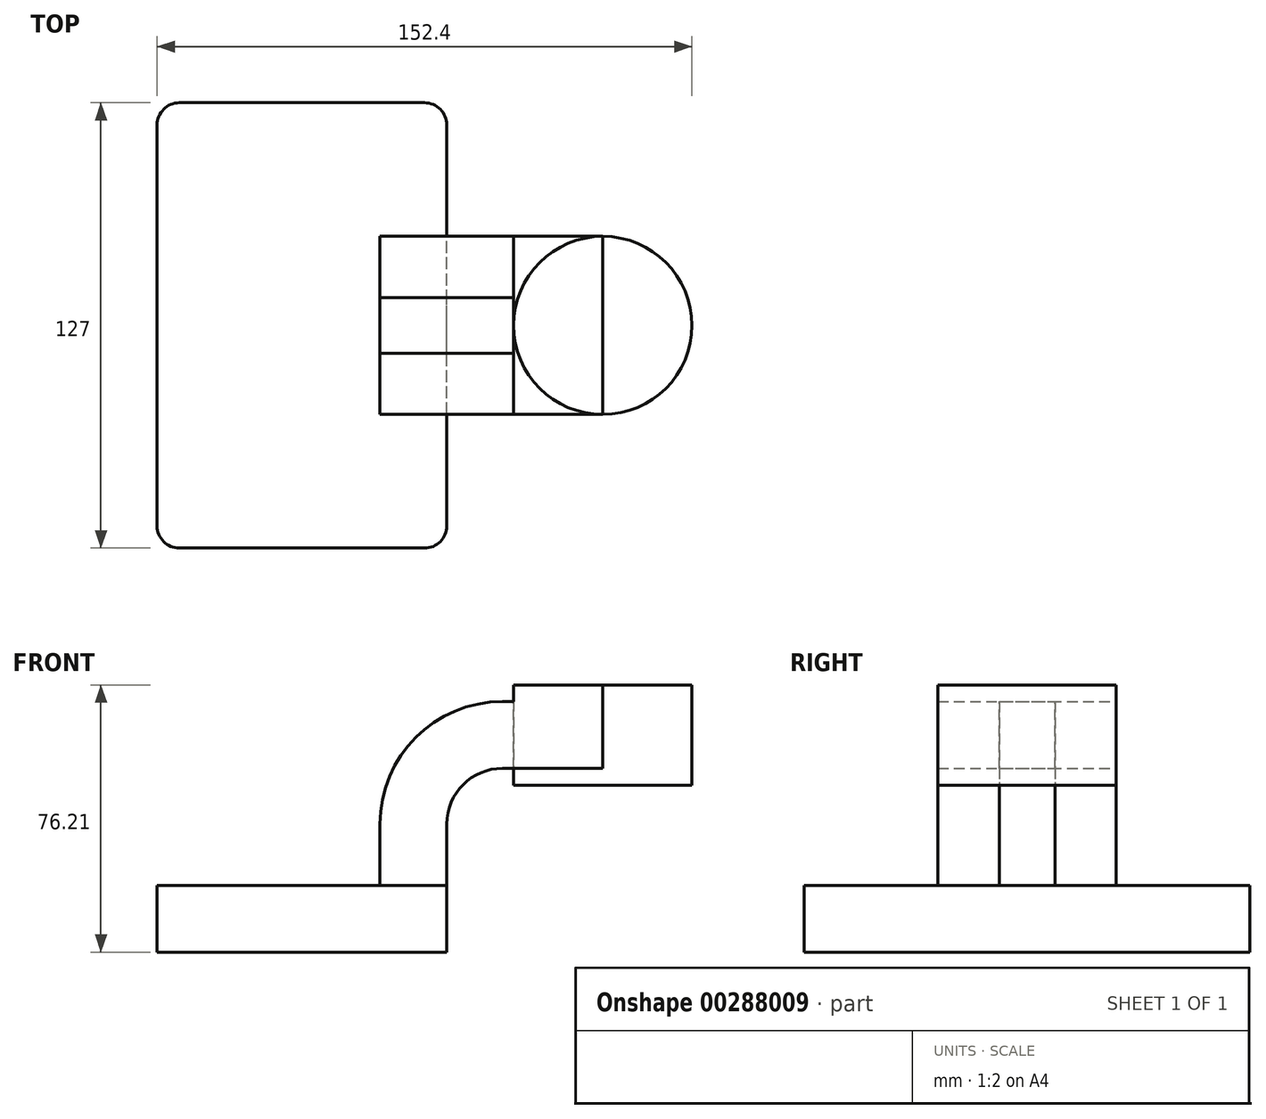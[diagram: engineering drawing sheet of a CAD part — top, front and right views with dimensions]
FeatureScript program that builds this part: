
annotation { "Feature Type Name" : "Feature", "Feature Type Description" : "" }
export const myFeature = defineFeature(function(context is Context, id is Id, definition is map)
    precondition{}
    {
        {
            var Q0;
            Q0=qCreatedBy(makeId("Front.planeOp"),FACE);
            var sketch = newSketch(context, id + "F0", { "sketchPlane" : qUnion([Q0])});
            skLineSegment(sketch, "E0.bottom", {"start": v(-41.28, -9.52) * mm, "end": v(41.28, -9.52) * mm});
            skLineSegment(sketch, "E0.top", {"start": v(-41.28, 9.53) * mm, "end": v(41.28, 9.53) * mm});
            skLineSegment(sketch, "E0.left", {"start": v(-41.27, -9.52) * mm, "end": v(-41.28, 9.53) * mm});
            skLineSegment(sketch, "E0.right", {"start": v(41.28, -9.52) * mm, "end": v(41.28, 9.53) * mm});
            skPoint(sketch, "E0.middle", {"position": v(0, 0) * mm});
            skLineSegment(sketch, "E1", {"start": v(41.27, 9.53) * mm, "end": v(41.27, 27) * mm});
            skArc(sketch, "E2", {"start": v(41.27, 27) * mm, "mid": v(45.92, 38.23) * mm, "end": v(57.15, 42.88) * mm});
            skLineSegment(sketch, "E3", {"start": v(57.15, 42.88) * mm, "end": v(85.73, 42.88) * mm});
            skLineSegment(sketch, "E4.bottom", {"start": v(60.33, 38.1) * mm, "end": v(111.13, 38.1) * mm});
            skLineSegment(sketch, "E4.top", {"start": v(60.33, 66.67) * mm, "end": v(111.12, 66.67) * mm});
            skLineSegment(sketch, "E4.left", {"start": v(60.33, 38.1) * mm, "end": v(60.33, 66.67) * mm});
            skLineSegment(sketch, "E4.right", {"start": v(111.13, 38.1) * mm, "end": v(111.12, 66.67) * mm});
            skPoint(sketch, "E4.middle", {"position": v(85.73, 52.39) * mm});
            skLineSegment(sketch, "E5.0", {"start": v(57.15, 61.93) * mm, "end": v(85.62, 61.93) * mm});
            skArc(sketch, "E5.1", {"start": v(22.22, 27) * mm, "mid": v(32.45, 51.7) * mm, "end": v(57.15, 61.93) * mm});
            skLineSegment(sketch, "E5.2", {"start": v(22.22, 9.53) * mm, "end": v(22.22, 27) * mm});
            skFitSpline(sketch, "E6", {"points": [v(-41.28, 9.53) * mm, v(57.15, 61.93) * mm], "startDerivative": vector(69, 130.5) * mm, "endDerivative": vector(97.75, -7.46) * mm});
            skPoint(sketch, "E7.endSnap0", {"position": v(85.72, 66.67) * mm});
            skPoint(sketch, "E8", {"position": v(85.73, 38.1) * mm});
            skLineSegment(sketch, "E9", {"start": v(85.72, 38.1) * mm, "end": v(85.72, 66.67) * mm});
            skSolve(sketch);
        }
        {
            var Q0;
            Q0=makeQuery(id+"F0.imprint","IMPRINT",FACE,{"disambiguationData":[TD([[makeQuery(id+"F0.imprint","IMPRINT",EDGE,{"derivedFrom":sQuery(id+"F0.wireOp",EDGE,"E0.bottom")}),1.0]])]});
            extrude(context, id + "F1", {"entities" : qUnion([Q0]), "endBound" : BoundingType.SYMMETRIC, "depth" : 127 * mm});
        }
        {
            var Q0;
            {var subQ2=sQuery(id+"F0.wireOp",EDGE,"E1");Q0=makeQuery(id+"F0.imprint","IMPRINT",FACE,{"disambiguationData":[TD([[makeQuery(id+"F0.imprint","IMPRINT",EDGE,{"derivedFrom":subQ2}),1.0]])]});}
            var Q1;
            {var subQ0=sQuery(id+"F0.wireOp",EDGE,"E7");var subQ1=sQuery(id+"F0.wireOp",EDGE,"E3");var subQ2=makeQuery(id+"F0.imprint","INTERSECT",VERTEX,{"derivedFrom":[subQ1,subQ0]});Q1=makeQuery(id+"F0.imprint","IMPRINT",FACE,{"disambiguationData":[TD([[makeQuery(id+"F0.imprint","IMPRINT",EDGE,{"disambiguationData":[TD([[subQ2,1.0]])],"derivedFrom":subQ1}),1.0]])]});}
            extrude(context, id + "F2", {"entities" : qUnion([Q0, Q1]), "endBound" : BoundingType.SYMMETRIC, "depth" : 50.8 * mm});
        }
        {
            var Q0;
            Q0=makeQuery(id+"F0.imprint","IMPRINT",FACE,{"disambiguationData":[TD([[makeQuery(id+"F0.imprint","IMPRINT",EDGE,{"derivedFrom":sQuery(id+"F0.wireOp",EDGE,"E5.1")}),1.0]])]});
            extrude(context, id + "F3", {"entities" : qUnion([Q0]), "endBound" : BoundingType.SYMMETRIC, "depth" : 15.88 * mm});
        }
        {
            var Q0;
            {var subQ4=sQuery(id+"F0.wireOp",EDGE,"E4.right");Q0=makeQuery(id+"F0.imprint","IMPRINT",FACE,{"disambiguationData":[TD([[makeQuery(id+"F0.imprint","IMPRINT",EDGE,{"derivedFrom":subQ4}),1.0]])]});}
            var Q1;
            Q1=sQuery(id+"F0.wireOp",EDGE,"E9");
            revolve(context, id + "F4", {"entities" : qUnion([Q0]), "axis" : qUnion([Q1]), "revolveType" : RevolveType.FULL});
        }
        {
            var Q0;
            Q0=makeQuery(id+"F1.opExtrude","CAP_EDGE",EDGE,{"disambiguationData":[OSD([sQuery(id+"F0.wireOp",EDGE,"E0.right")])],"isStart":false});
            var Q1;
            Q1=makeQuery(id+"F1.opExtrude","CAP_EDGE",EDGE,{"disambiguationData":[OSD([sQuery(id+"F0.wireOp",EDGE,"E0.left")])],"isStart":false});
            var Q2;
            Q2=makeQuery(id+"F1.opExtrude","CAP_EDGE",EDGE,{"disambiguationData":[OSD([sQuery(id+"F0.wireOp",EDGE,"E0.right")])],"isStart":true});
            var Q3;
            Q3=makeQuery(id+"F1.opExtrude","CAP_EDGE",EDGE,{"disambiguationData":[OSD([sQuery(id+"F0.wireOp",EDGE,"E0.left")])],"isStart":true});
            fillet(context, id + "F5", {"entities" : qUnion([Q0, Q1, Q2, Q3]), "radius" : 6.35 * mm, "tangentPropagation" : true, "allowEdgeOverflow" : false});
        }
    });
